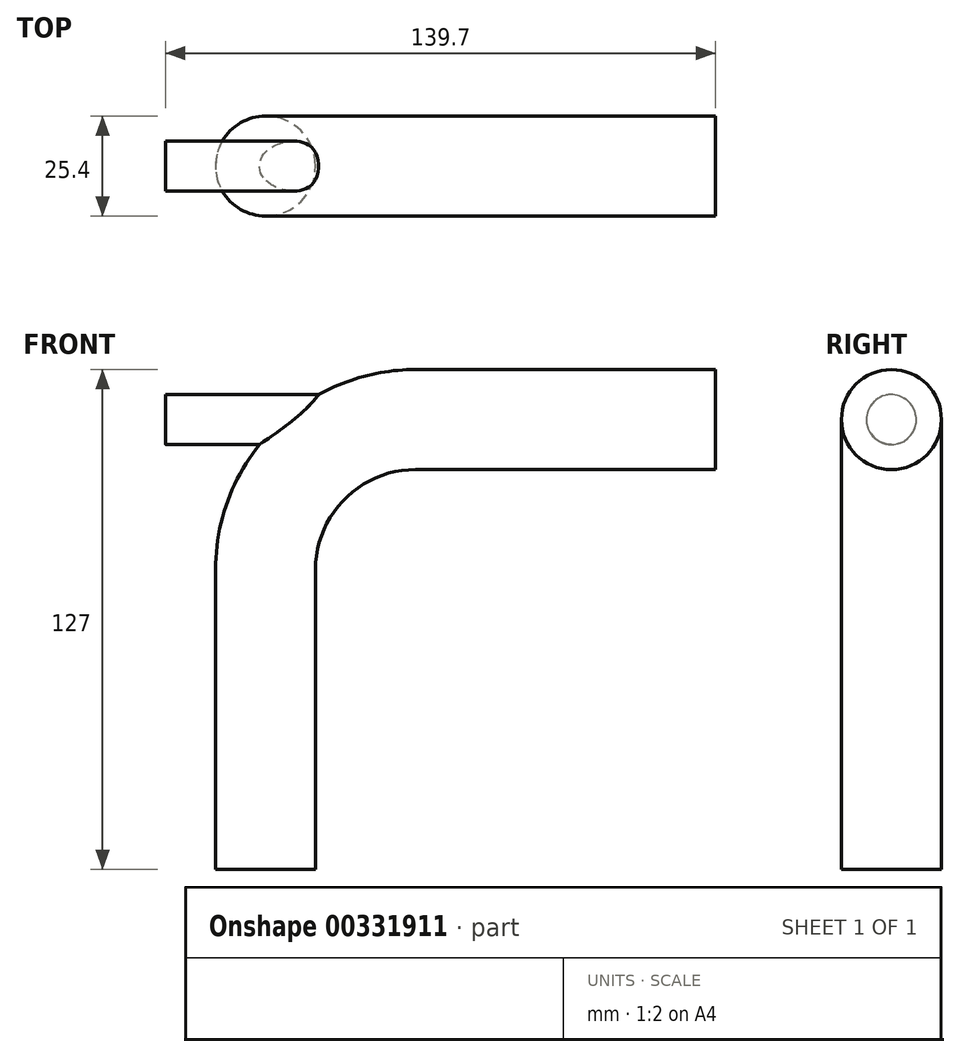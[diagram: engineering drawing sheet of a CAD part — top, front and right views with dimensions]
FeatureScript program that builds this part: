
annotation { "Feature Type Name" : "Feature", "Feature Type Description" : "" }
export const myFeature = defineFeature(function(context is Context, id is Id, definition is map)
    precondition{}
    {
        {
            var Q0;
            Q0=qCreatedBy(makeId("Front.planeOp"),FACE);
            var sketch = newSketch(context, id + "F0", { "sketchPlane" : qUnion([Q0])});
            skLineSegment(sketch, "E0", {"start": v(0, 0) * mm, "end": v(0, 76.2) * mm});
            skArc(sketch, "E1", {"start": v(38.1, 114.3) * mm, "mid": v(11.16, 103.14) * mm, "end": v(0, 76.2) * mm});
            skLineSegment(sketch, "E2", {"start": v(38.1, 114.3) * mm, "end": v(114.3, 114.3) * mm});
            skSolve(sketch);
        }
        {
            var Q0;
            Q0=qCreatedBy(makeId("Top.planeOp"),FACE);
            var sketch = newSketch(context, id + "F1", { "sketchPlane" : qUnion([Q0])});
            skCircle(sketch, "E3", {"center": v(0, 0) * mm, "radius": 12.7 * mm});
            skSolve(sketch);
        }
        {
            var Q0;
            Q0=makeQuery(id+"F1.imprint","IMPRINT",FACE,{"disambiguationData":[TD([[makeQuery(id+"F1.imprint","IMPRINT",EDGE,{"derivedFrom":sQuery(id+"F1.wireOp",EDGE,"E3")}),1.0]])]});
            var Q1;
            Q1 = qConstructionFilter(qBodyType(qCreatedBy(id + "F0" ,EDGE), BodyType.WIRE), ConstructionObject.NO);
            sweep(context, id + "F2", {"profiles" : qUnion([Q0]), "path" : qUnion([Q1])});
        }
        {
            var Q0;
            Q0=qCreatedBy(makeId("Right.planeOp"),FACE);
            cPlane(context, id + "F3", {"entities" : qUnion([Q0]), "cplaneType" : CPlaneType.OFFSET, "offset" : 25.4 * mm, "oppositeDirection" : true, "width" : 152.4 * mm, "height" : 152.4 * mm});
        }
        {
            var Q0;
            Q0=qCreatedBy(id+"F3.planeOp",FACE);
            var sketch = newSketch(context, id + "F4", { "sketchPlane" : qUnion([Q0])});
            skCircle(sketch, "E4", {"center": v(0, 114.3) * mm, "radius": 6.35 * mm});
            skSolve(sketch);
        }
        {
            var Q0;
            Q0=makeQuery(id+"F4.imprint","IMPRINT",FACE,{"disambiguationData":[TD([[makeQuery(id+"F4.imprint","IMPRINT",EDGE,{"derivedFrom":sQuery(id+"F4.wireOp",EDGE,"E4")}),1.0]])]});
            extrude(context, id + "F5", {"entities" : qUnion([Q0]), "operationType" : NewBodyOperationType.ADD, "depth" : 76.2 * mm});
        }
    });
